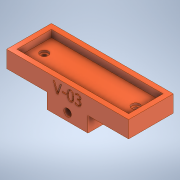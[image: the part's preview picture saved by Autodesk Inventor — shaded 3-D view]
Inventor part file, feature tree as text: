
AUTODESK INVENTOR PART (.ipt)
format: ipt  version: 2021.1 (Build 251245010, 245A)  size: 302,080 bytes
history: native  units: in
note: dims shown in document units (in); Inventor stores cm internally (conversion verified against a paired STEP export)
features: sketch x8, extrude x5, hole x4, projected_geometry x1
ambient origin geometry x8: Origin, YZ Plane, XZ Plane, XY Plane, X Axis, Y Axis, Z Axis, Center Point
bodies: Solid1 (feature_tree)
feature tree (18):
  sketch  "Sketch1"  dims[d0=1.7in d1=5.5in]
  extrude  "Extrusion1"  Depth=5.5in
  extrude  "Extrusion2"  Depth=0.25in
  hole  "Hole1"  [1 undecoded]
  extrude  "Extrusion6"  TaperAngle=0.0deg  [1 undecoded]
  extrude  "Extrusion7"  Depth=0.5in
  hole  "Hole2"  [1 undecoded]
  hole  "Hole3"  [1 undecoded]
  hole  "Hole4"  [1 undecoded]
  extrude  "Extrusion8"  TaperAngle=0.0deg  [1 undecoded]
  sketch  "Sketch2"  dims[d2=0.25in d3=0.25in]
  sketch  "Sketch5"  dims[d4=0.475in d5=0.0in]
  sketch  "Sketch6"  dims[d6=0.35in d7=0.0in]
  projected_geometry  "Projected Loop1"
  sketch  "Sketch7"  dims[d8=0.5in d9=0.5in]
  sketch  "Sketch9"  dims[d10=0.201in d11=0.75in d12=0.4in d13=0.1in d14=0.5635in d15=1.0in d16=0.8108in d17=0.375in]
  sketch  "Sketch10"  dims[d24=0.375in d27=2.0in]
  sketch  "Sketch11"  dims[d28=2.2in d29=0.75in d30=0.0in d31=0.375in d32=0.5in d33=0.0in d34=0.375in d35=1.0in d36=0.7333in d37=0.7874in d39=0.7333in d40=0.3937in d42=1.0in d44=0.201in d45=0.75in d46=0.257in d47=0.25in d48=0.5635in d49=1.0in d50=0.8108in d60=0.375in d61=0.7333in d62=0.7874in d64=0.7333in d65=0.3937in d67=1.0in d69=0.201in d70=0.75in d71=0.257in d72=0.375in d73=0.5635in d74=1.0in d75=0.8108in d76=0.375in d77=0.201in d78=0.75in d79=0.257in d80=0.375in d81=0.5635in d82=1.0in d83=0.8108in d84=0.1in d85=0.0in]
note: 6 required parameter values undecoded (feature->parameter linkage not recoverable at this tier; creation-order binding heuristic only, values carry confidence <= 0.55)
